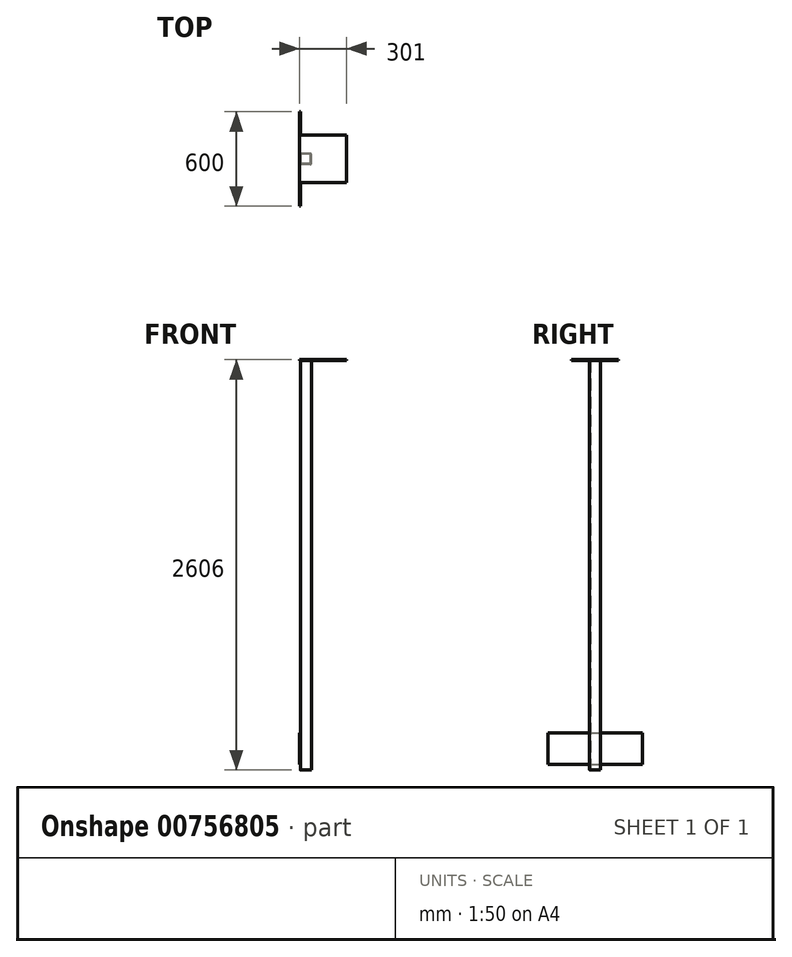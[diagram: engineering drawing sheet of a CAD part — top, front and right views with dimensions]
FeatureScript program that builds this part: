
annotation { "Feature Type Name" : "Feature", "Feature Type Description" : "" }
export const myFeature = defineFeature(function(context is Context, id is Id, definition is map)
    precondition{}
    {
        {
            var Q0;
            Q0=qCreatedBy(makeId("Front.planeOp"),FACE);
            var sketch = newSketch(context, id + "F0", { "sketchPlane" : qUnion([Q0])});
            skLineSegment(sketch, "E0.bottom", {"start": v(14.09, 2537.1) * mm, "end": v(-55.91, 2537.1) * mm});
            skLineSegment(sketch, "E0.top", {"start": v(14.09, -62.9) * mm, "end": v(-55.91, -62.9) * mm});
            skLineSegment(sketch, "E0.left", {"start": v(14.09, 2537.1) * mm, "end": v(14.09, -62.9) * mm});
            skLineSegment(sketch, "E0.right", {"start": v(-55.91, 2537.1) * mm, "end": v(-55.91, -62.9) * mm});
            skSolve(sketch);
        }
        {
            var Q0;
            Q0 = qSketchRegion(id + "F0", true);
            extrude(context, id + "F1", {"entities" : qUnion([Q0]), "depth" : 70 * mm, "offsetDistance" : 25 * mm});
        }
        {
            var Q0;
            Q0=makeQuery(id+"F1.opExtrude","SWEPT_FACE",FACE,{"disambiguationData":[OSD([sQuery(id+"F0.wireOp",EDGE,"E0.top")])]});
            var sketch = newSketch(context, id + "F2", { "sketchPlane" : qUnion([Q0])});
            skLineSegment(sketch, "E1.bottom", {"start": v(9.09, 65) * mm, "end": v(-50.91, 65) * mm});
            skLineSegment(sketch, "E1.top", {"start": v(9.09, 5) * mm, "end": v(-50.91, 5) * mm});
            skLineSegment(sketch, "E1.left", {"start": v(9.09, 65) * mm, "end": v(9.09, 5) * mm});
            skLineSegment(sketch, "E1.right", {"start": v(-50.91, 65) * mm, "end": v(-50.91, 5) * mm});
            skSolve(sketch);
        }
        {
            var Q0;
            Q0 = qSketchRegion(id + "F2", true);
            extrude(context, id + "F3", {"entities" : qUnion([Q0]), "operationType" : NewBodyOperationType.REMOVE, "endBound" : BoundingType.UP_TO_NEXT, "oppositeDirection" : true, "depth" : 25 * mm, "offsetDistance" : 25 * mm});
        }
        {
            var Q0;
            Q0=makeQuery(id+"F1.opExtrude","SWEPT_FACE",FACE,{"disambiguationData":[OSD([sQuery(id+"F0.wireOp",EDGE,"E0.right")])]});
            var sketch = newSketch(context, id + "F4", { "sketchPlane" : qUnion([Q0])});
            skLineSegment(sketch, "E2.bottom", {"start": v(335, -27.9) * mm, "end": v(-265, -27.9) * mm});
            skLineSegment(sketch, "E2.top", {"start": v(335, 172.1) * mm, "end": v(-265, 172.1) * mm});
            skLineSegment(sketch, "E2.left", {"start": v(335, -27.9) * mm, "end": v(335, 172.1) * mm});
            skLineSegment(sketch, "E2.right", {"start": v(-265, -27.9) * mm, "end": v(-265, 172.1) * mm});
            skSolve(sketch);
        }
        {
            var Q0;
            Q0 = qSketchRegion(id + "F4", true);
            extrude(context, id + "F5", {"entities" : qUnion([Q0]), "operationType" : NewBodyOperationType.ADD, "depth" : 6 * mm, "offsetDistance" : 25 * mm});
        }
        {
            var Q0;
            Q0=makeQuery(id+"F1.opExtrude","CAP_EDGE",EDGE,{"disambiguationData":[OSD([sQuery(id+"F0.wireOp",EDGE,"E0.left")])],"isStart":true});
            var Q1;
            Q1=makeQuery(id+"F1.opExtrude","CAP_EDGE",EDGE,{"disambiguationData":[OSD([sQuery(id+"F0.wireOp",EDGE,"E0.left")])],"isStart":false});
            var Q2;
            {var subQ0=sQuery(id+"F0.wireOp",EDGE,"E0.right");var subQ1=sQuery(id+"F0.wireOp",EDGE,"E0.bottom");var subQ2=makeQuery(id+"F1.opExtrude","CAP_FACE",FACE,{"disambiguationData":[OSD([subQ1,sQuery(id+"F0.wireOp",EDGE,"E0.top"),sQuery(id+"F0.wireOp",EDGE,"E0.left"),subQ0])],"isStart":true});var subQ4=makeQuery(id+"F1.opExtrude","SWEPT_FACE",FACE,{"disambiguationData":[OSD([subQ0])]});Q2=makeQuery(id+"F5.boolean.opBoolean","SPLIT",EDGE,{"disambiguationData":[topologyDisambiguationEdgeConnected([subQ2,subQ4]),TD([makeQuery(id+"F1.opExtrude","SWEPT_FACE",FACE,{"disambiguationData":[OSD([subQ1])]})])],"derivedFrom":makeQuery(id+"F1.opExtrude","CAP_EDGE",EDGE,{"disambiguationData":[OSD([subQ0])],"isStart":true})});}
            var Q3;
            {var subQ0=sQuery(id+"F0.wireOp",EDGE,"E0.right");var subQ1=sQuery(id+"F0.wireOp",EDGE,"E0.bottom");var subQ2=makeQuery(id+"F1.opExtrude","CAP_FACE",FACE,{"disambiguationData":[OSD([subQ1,sQuery(id+"F0.wireOp",EDGE,"E0.top"),sQuery(id+"F0.wireOp",EDGE,"E0.left"),subQ0])],"isStart":false});var subQ4=makeQuery(id+"F1.opExtrude","SWEPT_FACE",FACE,{"disambiguationData":[OSD([subQ0])]});Q3=makeQuery(id+"F5.boolean.opBoolean","SPLIT",EDGE,{"disambiguationData":[topologyDisambiguationEdgeConnected([subQ2,subQ4]),TD([makeQuery(id+"F1.opExtrude","SWEPT_FACE",FACE,{"disambiguationData":[OSD([subQ1])]})])],"derivedFrom":makeQuery(id+"F1.opExtrude","CAP_EDGE",EDGE,{"disambiguationData":[OSD([subQ0])],"isStart":false})});}
            fillet(context, id + "F6", {"entities" : qUnion([Q0, Q1, Q2, Q3]), "tangentPropagation" : true, "radius" : 5 * mm, "defaultsChanged" : false, "vertexSettings" : [], "allowEdgeOverflow" : false});
        }
        {
            var Q0;
            Q0=makeQuery(id+"F1.opExtrude","SWEPT_FACE",FACE,{"disambiguationData":[OSD([sQuery(id+"F0.wireOp",EDGE,"E0.bottom")])]});
            var sketch = newSketch(context, id + "F7", { "sketchPlane" : qUnion([Q0])});
            skLineSegment(sketch, "E3.bottom", {"start": v(-60.91, 115) * mm, "end": v(239.09, 115) * mm});
            skLineSegment(sketch, "E3.top", {"start": v(-60.91, -185) * mm, "end": v(239.09, -185) * mm});
            skLineSegment(sketch, "E3.left", {"start": v(-60.91, 115) * mm, "end": v(-60.91, -185) * mm});
            skLineSegment(sketch, "E3.right", {"start": v(239.09, 115) * mm, "end": v(239.09, -185) * mm});
            skSolve(sketch);
        }
        {
            var Q0;
            Q0 = qSketchRegion(id + "F7", true);
            extrude(context, id + "F8", {"entities" : qUnion([Q0]), "operationType" : NewBodyOperationType.ADD, "depth" : 6 * mm, "offsetDistance" : 25 * mm});
        }
    });
